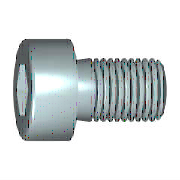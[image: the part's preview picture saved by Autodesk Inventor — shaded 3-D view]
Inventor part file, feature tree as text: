
AUTODESK INVENTOR PART (.ipt)
format: ipt  version: 2022 (Build 260153000, 153)  size: 198,144 bytes
history: native  units: mm (DEFAULTED — no unit token found)
features: sketch x2, extrude x1, plane x1, fillet x1
ambient origin geometry x7: Origin, YZ Plane, XY Plane, X Axis, Y Axis, Z Axis, Center Point
bodies: Solid1 (feature_tree), Body (feature_tree)
feature tree (5):
  extrude  "Slot"  Depth=6.0mm
  plane  "Work Plane1"
  fillet  "Fillet2"  Radius=6.0mm
  sketch  "Sketch1"  dims[d1=13.0mm d2=0.61355mm d3=6.0mm]
  sketch  "Sketch2"  dims[d4=3.3mm d5=60.0deg d6=6.0mm d7=5.3865mm d8=5.773503mm d9=10.0mm d10=90.0deg d11=10.0mm d12=0.0mm d13=13.0mm d14=0.0mm d15=0.61345mm d16=0.61345mm d17=0.6mm d19=0.0mm d26=16.0mm d27=45.0deg d28=0.0mm d29=0.0mm d30=0.1mm]
